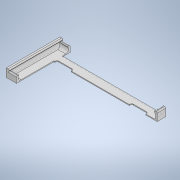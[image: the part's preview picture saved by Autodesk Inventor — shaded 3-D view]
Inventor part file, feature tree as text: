
AUTODESK INVENTOR PART (.ipt)
format: ipt  version: 2020 (Build 240168000, 168)  size: 355,328 bytes
history: native  units: in
note: dims shown in document units (in); Inventor stores cm internally (conversion verified against a paired STEP export)
features: other x3, sketch x3, projected_geometry x2, extrude x1
ambient origin geometry x8: Origin, YZ Plane, XZ Plane, XY Plane, X Axis, Y Axis, Z Axis, Center Point
bodies: Solid1 (feature_tree)
feature tree (9):
  other  "Part9 scaled.ipt"
  extrude  "Extrusion1"  TaperAngle=0.0deg  [1 undecoded]
  other  "Solid1::Part9 scaled.ipt"
  other  "TaggingFeature1"
  sketch  "Sketch22"
  sketch  "Sketch23"
  sketch  "Sketch3"  dims[d0=0.3937in d1=0.0in d2=0.0in]
  projected_geometry  "Projected Loop1"
  projected_geometry  "Projected Loop2"
note: 1 required parameter value undecoded (feature->parameter linkage not recoverable at this tier; creation-order binding heuristic only, values carry confidence <= 0.55)
